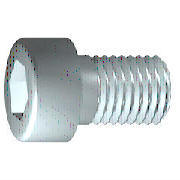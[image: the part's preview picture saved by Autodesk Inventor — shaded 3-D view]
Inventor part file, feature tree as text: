
AUTODESK INVENTOR PART (.ipt)
format: ipt  version: 2018 (Build 220112000, 112)  size: 196,608 bytes
history: native  units: mm (DEFAULTED — no unit token found)
features: sketch x2, extrude x1, plane x1, fillet x1
ambient origin geometry x7: Origin, YZ Plane, XY Plane, X Axis, Y Axis, Z Axis, Center Point
bodies: Solid1 (feature_tree), Body (feature_tree)
feature tree (5):
  extrude  "Slot"  Depth=5.0mm
  plane  "Work Plane1"
  fillet  "Fillet2"  Radius=5.0mm
  sketch  "Sketch1"  dims[d1=5.90924mm d2=0.49086mm d3=5.0mm]
  sketch  "Sketch2"  dims[d4=2.5mm d5=60.0deg d6=5.0mm d7=5.0mm d8=4.618802mm d9=8.5mm d10=90.0deg d11=10.0mm d12=0.0mm d13=5.90924mm d14=0.0mm d15=0.49076mm d16=0.49076mm d17=0.5mm d19=0.0mm d26=8.0mm d27=45.0deg d28=0.0mm d29=0.0mm d30=0.1mm]
